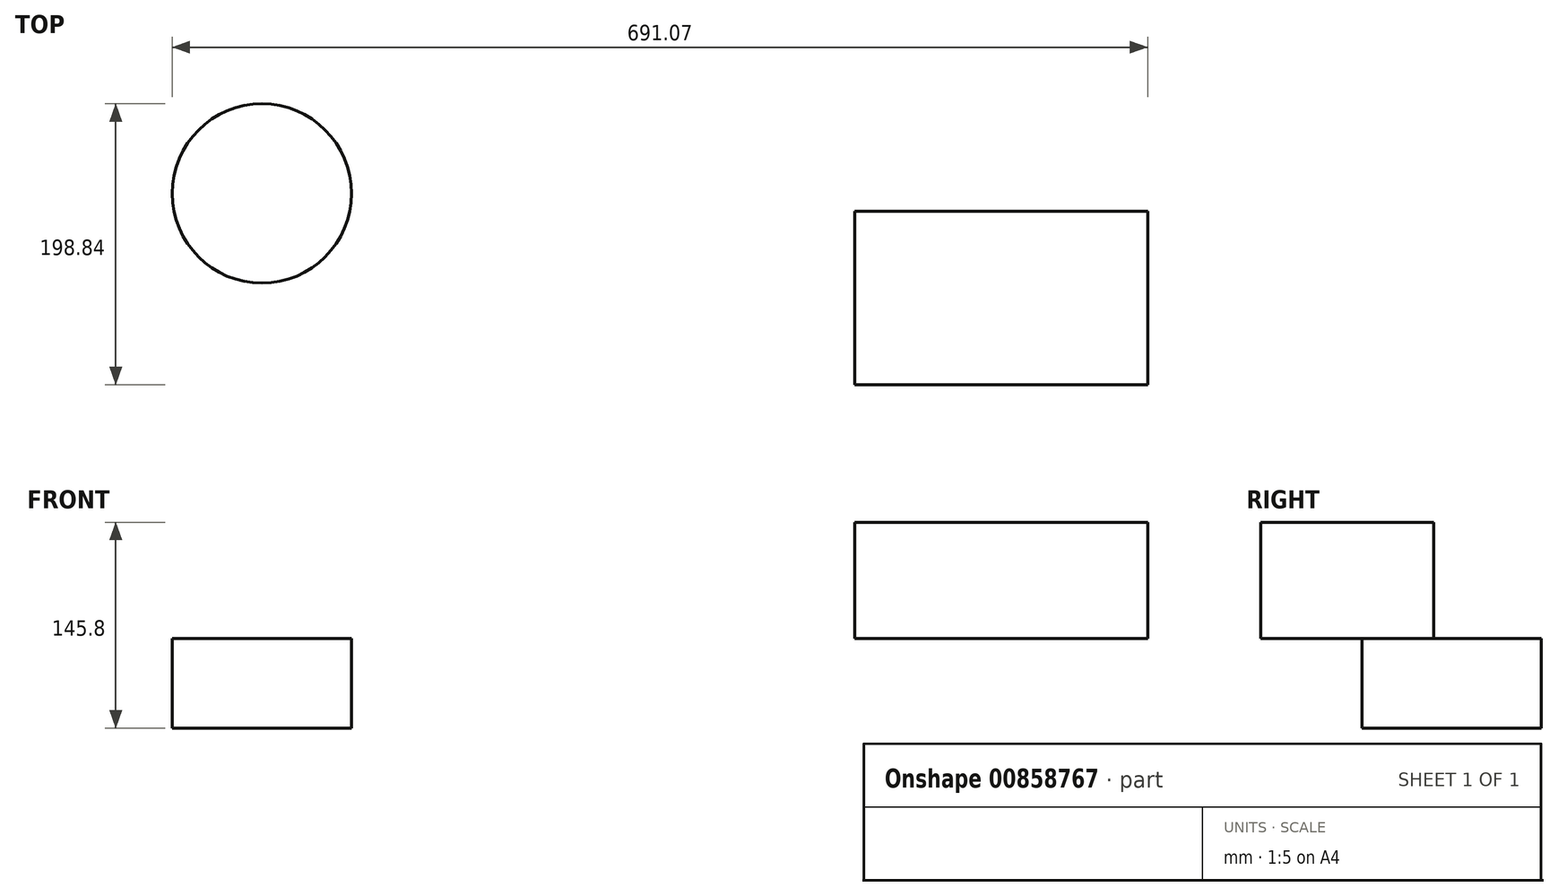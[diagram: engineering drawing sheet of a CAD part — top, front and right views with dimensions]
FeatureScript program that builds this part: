
annotation { "Feature Type Name" : "Feature", "Feature Type Description" : "" }
export const myFeature = defineFeature(function(context is Context, id is Id, definition is map)
    precondition{}
    {
        {
            var Q0;
            Q0=qCreatedBy(makeId("Top.planeOp"),FACE);
            var sketch = newSketch(context, id + "F0", { "sketchPlane" : qUnion([Q0])});
            skCircle(sketch, "E0", {"center": v(-311.54, 245.35) * mm, "radius": 63.5 * mm});
            skLineSegment(sketch, "E1.bottom", {"start": v(108.5, 232.64) * mm, "end": v(316.03, 232.64) * mm});
            skLineSegment(sketch, "E1.top", {"start": v(108.5, 110) * mm, "end": v(316.03, 110) * mm});
            skLineSegment(sketch, "E1.left", {"start": v(108.5, 232.64) * mm, "end": v(108.5, 110) * mm});
            skLineSegment(sketch, "E1.right", {"start": v(316.03, 232.64) * mm, "end": v(316.03, 110) * mm});
            skLineSegment(sketch, "E2", {"start": v(-335.96, -77.57) * mm, "end": v(-142.58, -143.6) * mm});
            skLineSegment(sketch, "E3", {"start": v(-142.58, -143.6) * mm, "end": v(-142.58, -336.98) * mm});
            skLineSegment(sketch, "E4", {"start": v(-142.58, -336.98) * mm, "end": v(-364.26, -372.36) * mm});
            skLineSegment(sketch, "E5", {"start": v(-364.26, -372.36) * mm, "end": v(-335.96, -77.57) * mm});
            skLineSegment(sketch, "E6", {"start": v(-277, -160.1) * mm, "end": v(-310.02, -292.17) * mm});
            skLineSegment(sketch, "E7", {"start": v(-310.02, -292.17) * mm, "end": v(-239, -309.93) * mm});
            skLineSegment(sketch, "E8", {"start": v(-239, -309.93) * mm, "end": v(-277, -160.1) * mm});
            skSolve(sketch);
        }
        {
            var Q0;
            Q0=makeQuery(id+"F0.imprint","IMPRINT",FACE,{"disambiguationData":[TD([[makeQuery(id+"F0.imprint","IMPRINT",EDGE,{"derivedFrom":sQuery(id+"F0.wireOp",EDGE,"E1.bottom")}),-1.0]])]});
            extrude(context, id + "F1", {"entities" : qUnion([Q0]), "depth" : 82.3 * mm, "offsetDistance" : 25.4 * mm});
        }
        {
            var Q0;
            Q0=makeQuery(id+"F0.imprint","IMPRINT",FACE,{"disambiguationData":[TD([[makeQuery(id+"F0.imprint","IMPRINT",EDGE,{"derivedFrom":sQuery(id+"F0.wireOp",EDGE,"E0")}),1.0]])]});
            extrude(context, id + "F2", {"entities" : qUnion([Q0]), "oppositeDirection" : true, "depth" : 63.5 * mm, "offsetDistance" : 25.4 * mm});
        }
    });
